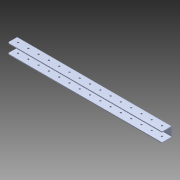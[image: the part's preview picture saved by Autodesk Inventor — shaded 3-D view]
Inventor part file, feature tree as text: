
AUTODESK INVENTOR PART (.ipt)
format: ipt  version: 2015 SP1 (Build 190203100, 203)  size: 397,312 bytes
history: native  units: in
note: dims shown in document units (in); Inventor stores cm internally (conversion verified against a paired STEP export)
features: projected_geometry x7, other x2, extrude x2, sketch x2, plane x1, mirror x1, imported_body x1
ambient origin geometry x8: Origin, YZ Plane, XZ Plane, XY Plane, X Axis, Y Axis, Z Axis, Center Point
bodies: Body1 (feature_tree)
feature tree (16):
  other  "Break-Corner1"
  other  "VersaFrame 1 x 1 x 1 x 0.090 C-Channel (59 length)(217-4107)1"
  plane  "Work Plane1"
  extrude  "Extrusion1"  Depth=1.0in TaperAngle=0.0deg
  mirror  "Mirror1"
  extrude  "Extrusion2"  [1 undecoded]
  imported_body  "Base1"
  sketch  "Sketch1"  dims[d0=11.0in d1=1.0in d2=0.0in]
  sketch  "Sketch3"  dims[d3=7.0in d4=0.0in]
  projected_geometry  "Projected Loop2"
  projected_geometry  "Projected Loop3"
  projected_geometry  "Projected Loop4"
  projected_geometry  "Projected Loop5"
  projected_geometry  "Projected Loop6"
  projected_geometry  "Projected Loop7"
  projected_geometry  "Projected Loop8"
note: 1 required parameter value undecoded (feature->parameter linkage not recoverable at this tier; creation-order binding heuristic only, values carry confidence <= 0.55)
